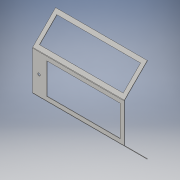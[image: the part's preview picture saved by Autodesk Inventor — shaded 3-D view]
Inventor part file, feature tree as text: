
AUTODESK INVENTOR PART (.ipt)
format: ipt  version: 2016 (Build 200138000, 138)  size: 175,104 bytes
history: native  units: mm
features: sheet_metal_op x7, sketch x7, other x6, hole x1
ambient origin geometry x8: Origin, YZ Plane, XZ Plane, XY Plane, X Axis, Y Axis, Z Axis, Center Point
bodies: Solid1 (feature_tree)
feature tree (21):
  sheet_metal_op  "Face1"
  sheet_metal_op  "Flange1"
  sheet_metal_op  "Flange2"
  hole  "Hole1"  [1 undecoded]
  sketch  "Sketch1"  dims[d0=700.0mm d1=300.0mm]
  other  "Plate1"
  sketch  "Sketch2"  dims[d2=3.0mm]
  other  "Plate2"
  sheet_metal_op  "Bend1"
  sheet_metal_op  "Corner1"
  sketch  "Sketch3"  dims[d3=3.0mm]
  other  "Plate3"
  sheet_metal_op  "Bend2"
  sheet_metal_op  "Corner2"
  sketch  "Sketch4"  dims[d4=1.5mm]
  sketch  "Sketch5"  dims[d5=6.0mm]
  sketch  "Sketch6"  dims[d6=3.0mm]
  sketch  "Sketch7"  dims[d7=250.0mm d8=-7.853982mm d9=3.0mm d10=12.0mm d11=3.0mm d12=3.0mm d13=3.0mm d14=1.5mm d15=6.0mm d16=3.0mm d17=250.0mm d18=-7.853982mm d19=3.0mm d20=12.0mm d21=3.0mm d22=3.0mm d23=20.0mm d24=50.0mm d25=150.0mm d26=20.0mm d27=6.0mm d28=4.0mm d29=2.0mm d30=90.0deg d31=3.0mm d32=20.594885mm d33=30.0mm d34=30.0mm d35=30.0mm d36=30.0mm d37=3.0mm d38=0.0mm d39=30.0mm d40=30.0mm d41=30.0mm d42=30.0mm d43=3.0mm d44=0.0mm d45=30.0mm d46=30.0mm d47=30.0mm d48=60.0mm d49=3.0mm d50=0.0mm]
  other  "Cut1"
  other  "Cut2"
  other  "Cut3"
note: 1 required parameter value undecoded (feature->parameter linkage not recoverable at this tier; creation-order binding heuristic only, values carry confidence <= 0.55)
